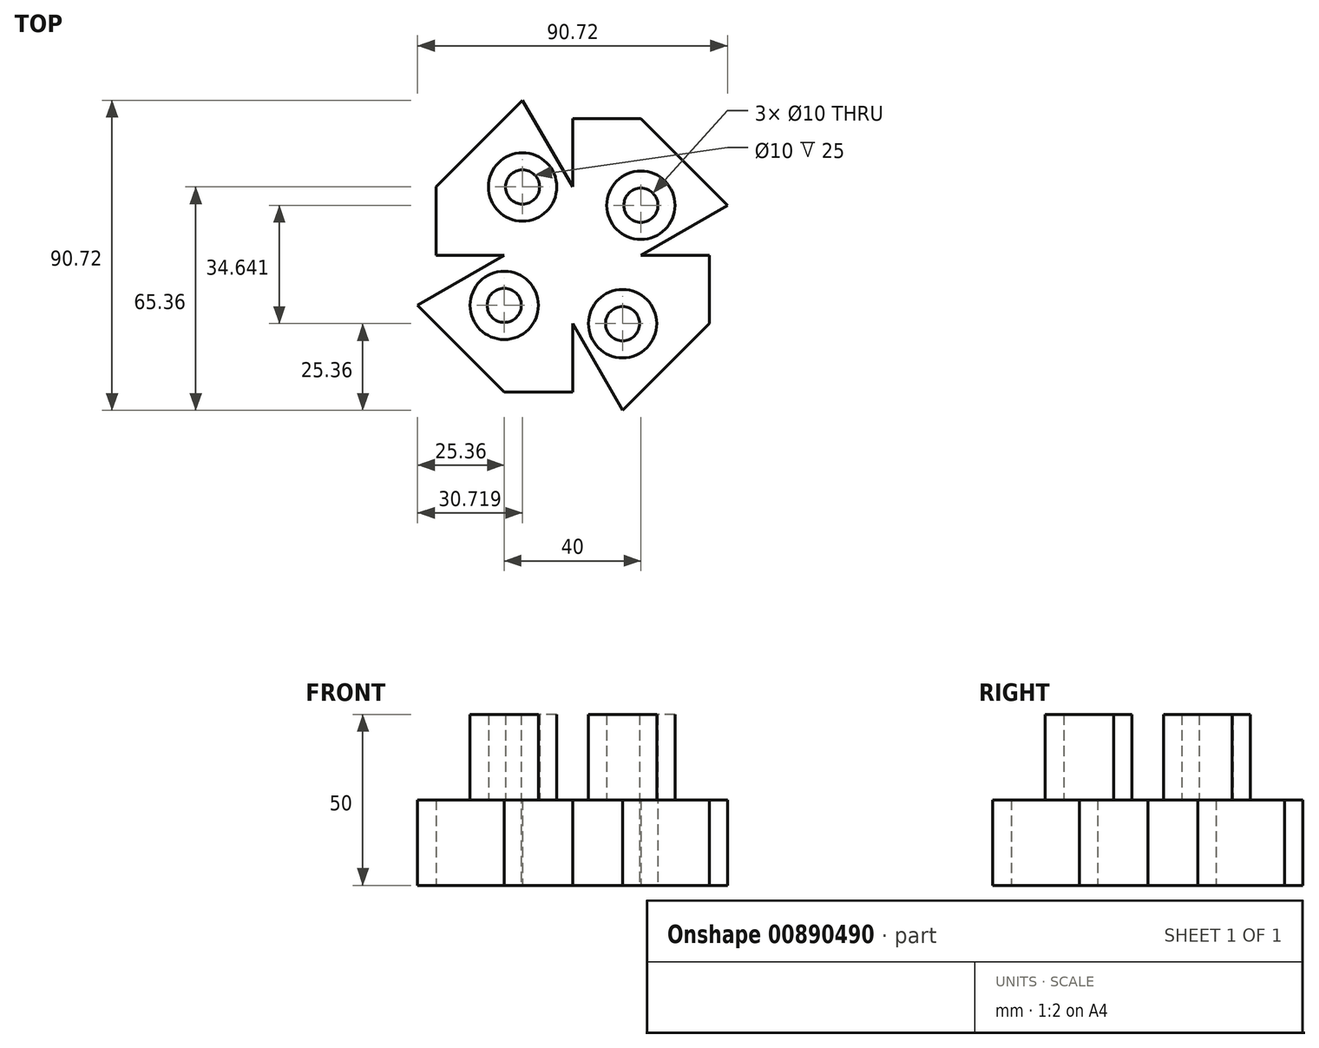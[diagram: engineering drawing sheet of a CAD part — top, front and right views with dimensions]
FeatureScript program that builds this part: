
annotation { "Feature Type Name" : "Feature", "Feature Type Description" : "" }
export const myFeature = defineFeature(function(context is Context, id is Id, definition is map)
    precondition{}
    {
        {
            var Q0;
            Q0=qCreatedBy(makeId("Top.planeOp"),FACE);
            var sketch = newSketch(context, id + "F0", { "sketchPlane" : qUnion([Q0])});
            skLineSegment(sketch, "E0", {"start": v(0, 0) * mm, "end": v(-40, 0) * mm});
            skLineSegment(sketch, "E1", {"start": v(-40, 0) * mm, "end": v(-40, 20) * mm});
            skLineSegment(sketch, "E2", {"start": v(-40, 20) * mm, "end": v(0, 20) * mm, "construction": true});
            skLineSegment(sketch, "E3", {"start": v(0, 20) * mm, "end": v(0, 0) * mm});
            skLineSegment(sketch, "E4", {"start": v(-40, 20) * mm, "end": v(-14.64, 45.36) * mm});
            skLineSegment(sketch, "E5", {"start": v(0, 20) * mm, "end": v(-14.64, 45.36) * mm});
            skLineSegment(sketch, "E6", {"start": v(-14.64, 45.36) * mm, "end": v(-14.64, 0) * mm, "construction": true});
            skCircle(sketch, "E7", {"center": v(-14.64, 20) * mm, "radius": 10 * mm});
            skArc(sketch, "E8", {"start": v(-17.22, 29.66) * mm, "mid": v(-33.65, 18.7) * mm, "end": v(-40, 0) * mm});
            skLineSegment(sketch, "E9.1.0", {"start": v(-20, -40) * mm, "end": v(-45.36, -14.64) * mm});
            skLineSegment(sketch, "E9.1.1", {"start": v(-45.36, -14.64) * mm, "end": v(0, -14.64) * mm, "construction": true});
            skLineSegment(sketch, "E9.1.2", {"start": v(0, 0) * mm, "end": v(0, -40) * mm});
            skLineSegment(sketch, "E9.1.3", {"start": v(-20, 0) * mm, "end": v(-45.36, -14.64) * mm});
            skLineSegment(sketch, "E9.1.4", {"start": v(-20, 0) * mm, "end": v(0, 0) * mm});
            skLineSegment(sketch, "E9.1.5", {"start": v(0, -40) * mm, "end": v(-20, -40) * mm});
            skLineSegment(sketch, "E9.1.6", {"start": v(-20, -40) * mm, "end": v(-20, 0) * mm, "construction": true});
            skCircle(sketch, "E9.1.7", {"center": v(-20, -14.64) * mm, "radius": 10 * mm});
            skArc(sketch, "E9.1.8", {"start": v(-29.66, -17.22) * mm, "mid": v(-18.7, -33.65) * mm, "end": v(0, -40) * mm});
            skLineSegment(sketch, "E9.2.0", {"start": v(40, -20) * mm, "end": v(14.64, -45.36) * mm});
            skLineSegment(sketch, "E9.2.1", {"start": v(14.64, -45.36) * mm, "end": v(14.64, 0) * mm, "construction": true});
            skLineSegment(sketch, "E9.2.2", {"start": v(0, 0) * mm, "end": v(40, 0) * mm});
            skLineSegment(sketch, "E9.2.3", {"start": v(0, -20) * mm, "end": v(14.64, -45.36) * mm});
            skLineSegment(sketch, "E9.2.4", {"start": v(0, -20) * mm, "end": v(0, 0) * mm});
            skLineSegment(sketch, "E9.2.5", {"start": v(40, 0) * mm, "end": v(40, -20) * mm});
            skLineSegment(sketch, "E9.2.6", {"start": v(40, -20) * mm, "end": v(0, -20) * mm, "construction": true});
            skCircle(sketch, "E9.2.7", {"center": v(14.64, -20) * mm, "radius": 10 * mm});
            skArc(sketch, "E9.2.8", {"start": v(17.22, -29.66) * mm, "mid": v(33.65, -18.7) * mm, "end": v(40, 0) * mm});
            skLineSegment(sketch, "E9.3.0", {"start": v(20, 40) * mm, "end": v(45.36, 14.64) * mm});
            skLineSegment(sketch, "E9.3.1", {"start": v(45.36, 14.64) * mm, "end": v(0, 14.64) * mm, "construction": true});
            skLineSegment(sketch, "E9.3.2", {"start": v(0, 0) * mm, "end": v(0, 40) * mm});
            skLineSegment(sketch, "E9.3.3", {"start": v(20, 0) * mm, "end": v(45.36, 14.64) * mm});
            skLineSegment(sketch, "E9.3.4", {"start": v(20, 0) * mm, "end": v(0, 0) * mm});
            skLineSegment(sketch, "E9.3.5", {"start": v(0, 40) * mm, "end": v(20, 40) * mm});
            skLineSegment(sketch, "E9.3.6", {"start": v(20, 40) * mm, "end": v(20, 0) * mm, "construction": true});
            skCircle(sketch, "E9.3.7", {"center": v(20, 14.64) * mm, "radius": 10 * mm});
            skArc(sketch, "E9.3.8", {"start": v(29.66, 17.22) * mm, "mid": v(18.7, 33.65) * mm, "end": v(0, 40) * mm});
            skPoint(sketch, "E9.center", {"position": v(0, 0) * mm});
            skCircle(sketch, "E10", {"center": v(-14.64, 20) * mm, "radius": 5 * mm});
            skPoint(sketch, "E10.first.point", {"position": v(-9.79, 18.79) * mm});
            skPoint(sketch, "E10.second.point", {"position": v(-19.57, 20.84) * mm});
            skPoint(sketch, "E10.third.point", {"position": v(-19.33, 21.73) * mm});
            skCircle(sketch, "E11", {"center": v(-20, -14.64) * mm, "radius": 5 * mm});
            skCircle(sketch, "E12", {"center": v(14.64, -20) * mm, "radius": 5 * mm});
            skCircle(sketch, "E13", {"center": v(20, 14.64) * mm, "radius": 5 * mm});
            skSolve(sketch);
        }
        {
            var Q0;
            Q0=makeQuery(id+"F0.imprint","IMPRINT",FACE,{"disambiguationData":[TD([[makeQuery(id+"F0.imprint","IMPRINT",EDGE,{"derivedFrom":sQuery(id+"F0.wireOp",EDGE,"E9.2.0")}),-1.0]])]});
            var Q1;
            Q1=makeQuery(id+"F0.imprint","IMPRINT",FACE,{"disambiguationData":[TD([[makeQuery(id+"F0.imprint","IMPRINT",EDGE,{"derivedFrom":sQuery(id+"F0.wireOp",EDGE,"E9.2.7")}),1.0]])]});
            var Q2;
            Q2=makeQuery(id+"F0.imprint","IMPRINT",FACE,{"disambiguationData":[TD([[makeQuery(id+"F0.imprint","IMPRINT",EDGE,{"derivedFrom":sQuery(id+"F0.wireOp",EDGE,"E9.1.0")}),-1.0]])]});
            var Q3;
            Q3=makeQuery(id+"F0.imprint","IMPRINT",FACE,{"disambiguationData":[TD([[makeQuery(id+"F0.imprint","IMPRINT",EDGE,{"derivedFrom":sQuery(id+"F0.wireOp",EDGE,"E9.1.7")}),1.0]])]});
            var Q4;
            Q4=makeQuery(id+"F0.imprint","IMPRINT",FACE,{"disambiguationData":[TD([[makeQuery(id+"F0.imprint","IMPRINT",EDGE,{"derivedFrom":sQuery(id+"F0.wireOp",EDGE,"E0")}),-1.0]])]});
            var Q5;
            Q5=makeQuery(id+"F0.imprint","IMPRINT",FACE,{"disambiguationData":[TD([[makeQuery(id+"F0.imprint","IMPRINT",EDGE,{"derivedFrom":sQuery(id+"F0.wireOp",EDGE,"E7")}),1.0]])]});
            var Q6;
            Q6=makeQuery(id+"F0.imprint","IMPRINT",FACE,{"disambiguationData":[TD([[makeQuery(id+"F0.imprint","IMPRINT",EDGE,{"derivedFrom":sQuery(id+"F0.wireOp",EDGE,"E10")}),1.0]])]});
            var Q7;
            Q7=makeQuery(id+"F0.imprint","IMPRINT",FACE,{"disambiguationData":[TD([[makeQuery(id+"F0.imprint","IMPRINT",EDGE,{"derivedFrom":sQuery(id+"F0.wireOp",EDGE,"E9.3.0")}),-1.0]])]});
            var Q8;
            Q8=makeQuery(id+"F0.imprint","IMPRINT",FACE,{"disambiguationData":[TD([[makeQuery(id+"F0.imprint","IMPRINT",EDGE,{"derivedFrom":sQuery(id+"F0.wireOp",EDGE,"E9.3.7")}),1.0]])]});
            extrude(context, id + "F1", {"entities" : qUnion([Q0, Q1, Q2, Q3, Q4, Q5, Q6, Q7, Q8]), "depth" : 25 * mm, "offsetDistance" : 25 * mm});
        }
        {
            var Q0;
            Q0=makeQuery(id+"F0.imprint","IMPRINT",FACE,{"disambiguationData":[TD([[makeQuery(id+"F0.imprint","IMPRINT",EDGE,{"derivedFrom":sQuery(id+"F0.wireOp",EDGE,"E7")}),1.0]])]});
            var Q1;
            Q1=makeQuery(id+"F0.imprint","IMPRINT",FACE,{"disambiguationData":[TD([[makeQuery(id+"F0.imprint","IMPRINT",EDGE,{"derivedFrom":sQuery(id+"F0.wireOp",EDGE,"E9.1.7")}),1.0]])]});
            var Q2;
            Q2=makeQuery(id+"F0.imprint","IMPRINT",FACE,{"disambiguationData":[TD([[makeQuery(id+"F0.imprint","IMPRINT",EDGE,{"derivedFrom":sQuery(id+"F0.wireOp",EDGE,"E9.2.7")}),1.0]])]});
            var Q3;
            Q3=makeQuery(id+"F0.imprint","IMPRINT",FACE,{"disambiguationData":[TD([[makeQuery(id+"F0.imprint","IMPRINT",EDGE,{"derivedFrom":sQuery(id+"F0.wireOp",EDGE,"E9.3.7")}),1.0]])]});
            extrude(context, id + "F2", {"entities" : qUnion([Q0, Q1, Q2, Q3]), "operationType" : NewBodyOperationType.ADD, "depth" : 50 * mm, "offsetDistance" : 25 * mm});
        }
    });
